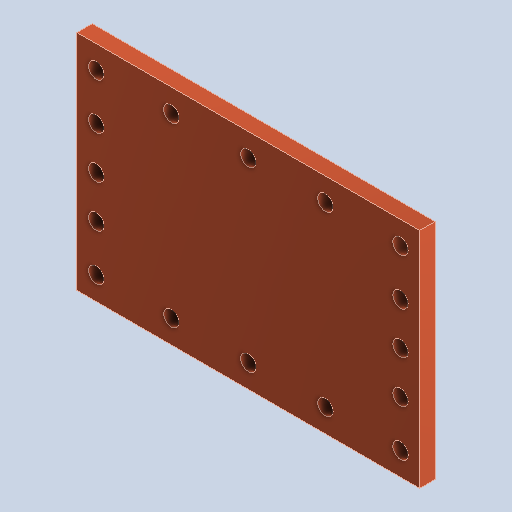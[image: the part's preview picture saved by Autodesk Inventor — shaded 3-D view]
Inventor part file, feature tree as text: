
AUTODESK INVENTOR PART (.ipt)
format: ipt  version: 2025.1 (Build 291241000, 241)  size: 135,680 bytes
history: native  units: mm
features: sketch x4, other x3, plane x1
ambient origin geometry x8: Origin, YZ Plane, XZ Plane, XY Plane, X Axis, Y Axis, Z Axis, Center Point
bodies: Volumenkörper1 (feature_tree)
feature tree (8):
  other  "1152.ipt"
  other  "Volumenkörper1::1152.ipt"
  other  "TaggingFeature1"
  sketch  "Skizze1"  dims[d0=10.0mm]
  sketch  "Skizze2"
  sketch  "Skizze3"
  sketch  "Skizze4"
  plane  "Arbeitsebene1"
